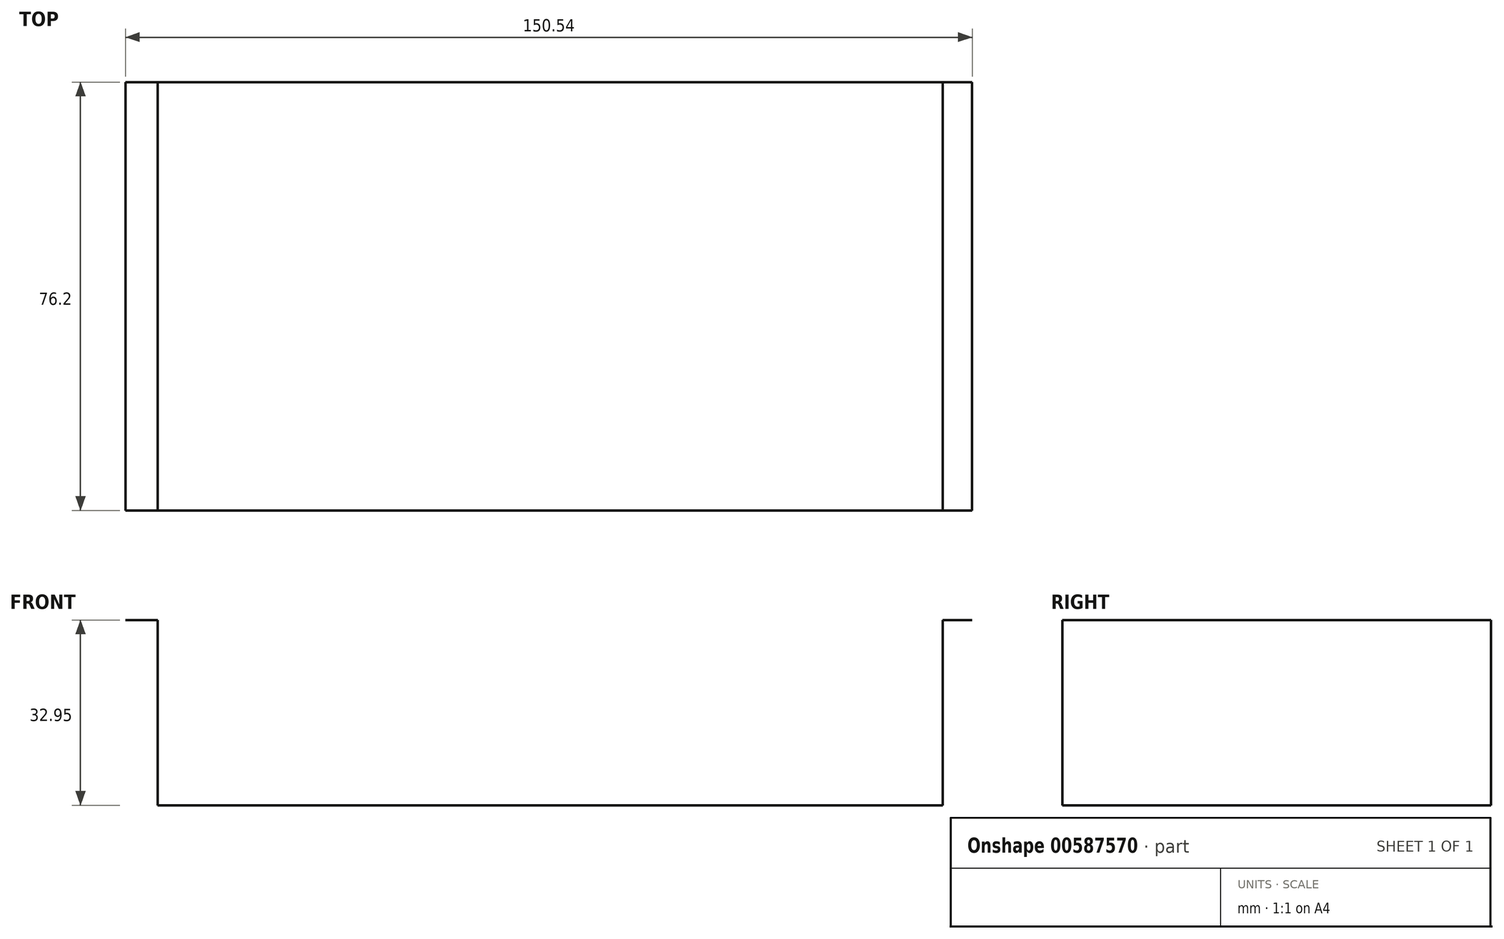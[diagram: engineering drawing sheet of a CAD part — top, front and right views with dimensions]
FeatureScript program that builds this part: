
annotation { "Feature Type Name" : "Feature", "Feature Type Description" : "" }
export const myFeature = defineFeature(function(context is Context, id is Id, definition is map)
    precondition{}
    {
        {
            var Q0;
            Q0=qCreatedBy(makeId("Front.planeOp"),FACE);
            var sketch = newSketch(context, id + "F0", { "sketchPlane" : qUnion([Q0])});
            skLineSegment(sketch, "E0", {"start": v(-74.52, 32.95) * mm, "end": v(-68.78, 32.95) * mm});
            skLineSegment(sketch, "E1", {"start": v(-68.78, 32.95) * mm, "end": v(-68.78, 0) * mm});
            skLineSegment(sketch, "E2", {"start": v(-68.78, 0) * mm, "end": v(70.77, 0) * mm});
            skLineSegment(sketch, "E3", {"start": v(70.77, 0) * mm, "end": v(70.77, 32.95) * mm});
            skLineSegment(sketch, "E4", {"start": v(70.77, 32.95) * mm, "end": v(76.02, 32.95) * mm});
            skSolve(sketch);
        }
        {
            var Q0;
            Q0 = qSketchRegion(id + "F0", true);
            var Q1;
            Q1=sQuery(id+"F0.wireOp",EDGE,"E0");
            var Q2;
            Q2=sQuery(id+"F0.wireOp",EDGE,"E1");
            var Q3;
            Q3=sQuery(id+"F0.wireOp",EDGE,"E2");
            var Q4;
            Q4=sQuery(id+"F0.wireOp",EDGE,"E3");
            var Q5;
            Q5=sQuery(id+"F0.wireOp",EDGE,"E4");
            extrude(context, id + "F1", {"entities" : qUnion([Q0]), "bodyType" : ToolBodyType.SURFACE, "surfaceEntities" : qUnion([Q1, Q2, Q3, Q4, Q5]), "oppositeDirection" : true, "depth" : 76.2 * mm, "offsetDistance" : 25.4 * mm});
        }
    });
